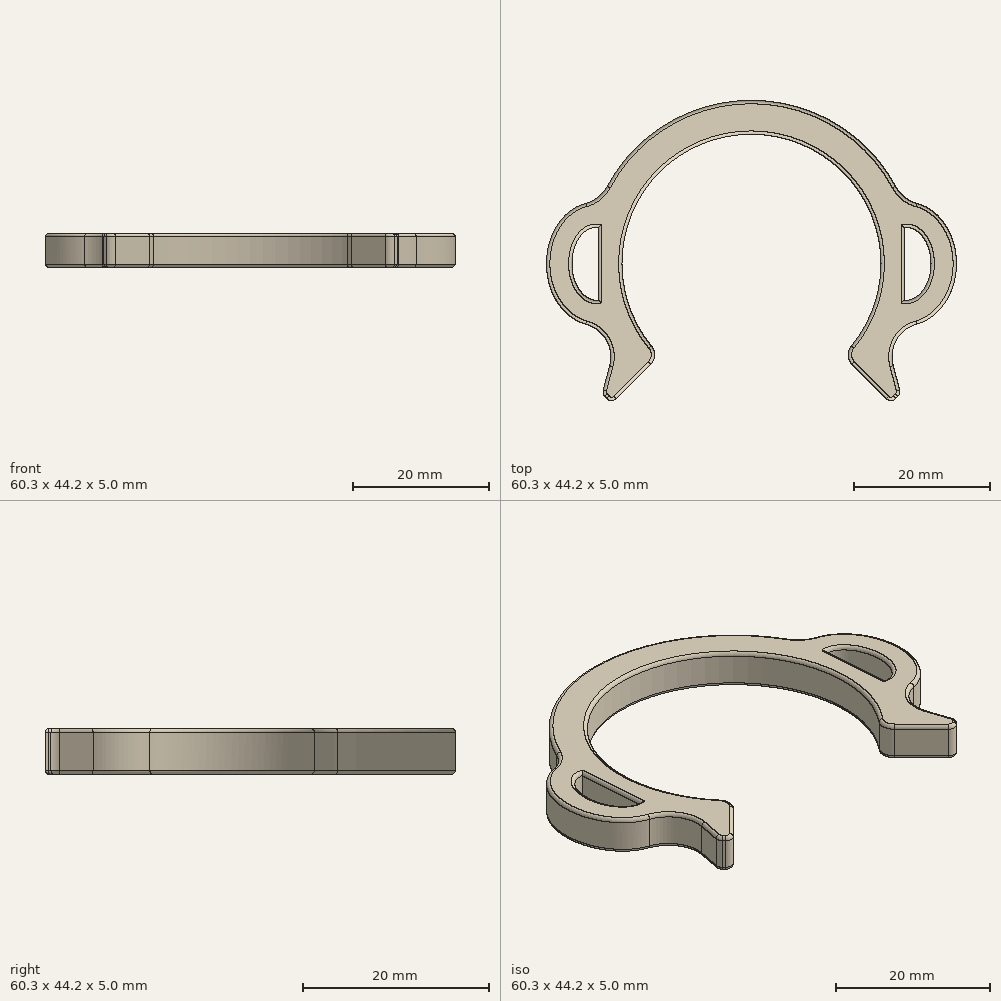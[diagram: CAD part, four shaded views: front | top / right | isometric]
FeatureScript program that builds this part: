
annotation { "Feature Type Name" : "Feature", "Feature Type Description" : "" }
export const myFeature = defineFeature(function(context is Context, id is Id, definition is map)
    precondition{}
    {
        {
            var Q0;
            Q0=qCreatedBy(makeId("Top.planeOp"),FACE);
            var sketch = newSketch(context, id + "F0", { "sketchPlane" : qUnion([Q0])});
            skCircle(sketch, "E0", {"center": v(0, 0) * mm, "radius": 18.75 * mm, "construction": true});
            skLineSegment(sketch, "E1", {"start": v(-22.75, 5.1) * mm, "end": v(-22.75, -5.1) * mm, "construction": true});
            skEllipticalArc(sketch, "E2", {"construction": true});
            skPoint(sketch, "E3", {"position": v(-22.75, 5.1) * mm});
            skPoint(sketch, "E4", {"position": v(-22.75, -5.1) * mm});
            skPoint(sketch, "E5", {"position": v(-26.15, 0) * mm});
            skLineSegment(sketch, "E6", {"start": v(0, 0) * mm, "end": v(0, 18.75) * mm, "construction": true});
            skEllipticalArc(sketch, "E7.MirrorCS", {"construction": true});
            skLineSegment(sketch, "E8.MirrorCS", {"start": v(22.75, 5.1) * mm, "end": v(22.75, -5.1) * mm, "construction": true});
            skCircle(sketch, "E9", {"center": v(-4, -23.75) * mm, "radius": 0.83 * mm, "construction": true});
            skArc(sketch, "E10", {"start": v(-13.47, -13.47) * mm, "mid": v(0, 19.05) * mm, "end": v(13.47, -13.47) * mm});
            skPoint(sketch, "E11", {"position": v(0, 19.05) * mm});
            skArc(sketch, "E12", {"start": v(0, 24.05) * mm, "mid": v(-12.35, 20.64) * mm, "end": v(-21.2, 11.36) * mm});
            skEllipticalArc(sketch, "E13", {});
            skPoint(sketch, "E14", {"position": v(-30.15, 0) * mm});
            skPoint(sketch, "E15", {"position": v(-22.75, 9.1) * mm});
            skLineSegment(sketch, "E16", {"start": v(-22.75, 5.1) * mm, "end": v(-22.75, 9.1) * mm, "construction": true});
            skLineSegment(sketch, "E17", {"start": v(-26.15, 0) * mm, "end": v(-30.15, 0) * mm, "construction": true});
            skPoint(sketch, "E18.visualSharp", {"position": v(-22.27, 9.08) * mm});
            skArc(sketch, "E18.filletArc", {"start": v(-24.32, 8.9) * mm, "mid": v(-22.5, 9.8) * mm, "end": v(-21.2, 11.36) * mm});
            skLineSegment(sketch, "E19.1", {"start": v(-22.5, 5.35) * mm, "end": v(-22.5, -5.35) * mm});
            skLineSegment(sketch, "E20", {"start": v(-13.47, -13.47) * mm, "end": v(-20.54, -20.54) * mm});
            skLineSegment(sketch, "E21", {"start": v(-20.54, -20.54) * mm, "end": v(-21.96, -19.13) * mm});
            skLineSegment(sketch, "E22", {"start": v(-21.96, -19.13) * mm, "end": v(-20.85, -15) * mm});
            skPoint(sketch, "E23.visualSharp", {"position": v(-18.92, -7.78) * mm});
            skArc(sketch, "E23.filletArc", {"start": v(-20.85, -15) * mm, "mid": v(-21.34, -11.22) * mm, "end": v(-24.36, -8.88) * mm});
            skArc(sketch, "E24.MirrorCS", {"start": v(0, 24.05) * mm, "mid": v(12.35, 20.64) * mm, "end": v(21.2, 11.36) * mm});
            skArc(sketch, "E25.MirrorCS", {"start": v(24.32, 8.9) * mm, "mid": v(22.5, 9.8) * mm, "end": v(21.2, 11.36) * mm});
            skEllipticalArc(sketch, "E26.MirrorCS", {});
            skArc(sketch, "E27.MirrorCS", {"start": v(20.85, -15) * mm, "mid": v(21.34, -11.22) * mm, "end": v(24.36, -8.88) * mm});
            skLineSegment(sketch, "E28.MirrorCS", {"start": v(21.96, -19.13) * mm, "end": v(20.85, -15) * mm});
            skLineSegment(sketch, "E29.MirrorCS", {"start": v(20.54, -20.54) * mm, "end": v(21.96, -19.13) * mm});
            skLineSegment(sketch, "E30.MirrorCS", {"start": v(13.47, -13.47) * mm, "end": v(20.54, -20.54) * mm});
            skLineSegment(sketch, "E31.MirrorCS", {"start": v(22.5, 5.35) * mm, "end": v(22.5, -5.35) * mm});
            skEllipticalArc(sketch, "E32", {});
            skLineSegment(sketch, "E33", {"start": v(26.4, 0) * mm, "end": v(26.15, 0) * mm, "construction": true});
            skLineSegment(sketch, "E34", {"start": v(22.75, 0) * mm, "end": v(22.5, 0) * mm, "construction": true});
            skLineSegment(sketch, "E35", {"start": v(-22.75, 0) * mm, "end": v(-22.5, 0) * mm, "construction": true});
            skEllipticalArc(sketch, "E36", {});
            skPoint(sketch, "E37", {"position": v(-26.4, 0) * mm});
            skCircle(sketch, "E38", {"center": v(4, -23.75) * mm, "radius": 0.83 * mm, "construction": true});
            skLineSegment(sketch, "E39", {"start": v(-4, -23.75) * mm, "end": v(4, -23.75) * mm, "construction": true});
            skLineSegment(sketch, "E40", {"start": v(0, 0) * mm, "end": v(0, -23.75) * mm, "construction": true});
            skPoint(sketch, "E41", {"position": v(0, -18.75) * mm});
            const initialGuessF0  = {"E2": [-0.02275, 0, 0, -1, 0.0051, 0.0034, 3.141592653589793, 0], "E7.MirrorCS": [0.02275, 0, 0, -1, 0.0051, 0.0034, 0, 3.141592653589793], "E13": [-0.02275, 0, 0, 1, 0.0091, 0.0074, 0.21327389126291205, 2.922477853467835], "E26.MirrorCS": [0.02275, 0, 0, 1, 0.0091, 0.0074, 3.3607074537117514, 6.069911415916674], "E32": [0.02275, 0, 0, 1, 0.005362593586465865, 0.00365, 3.073045835744844, 0.06854681784494943], "E36": [-0.02275, 0, 0, 1, 0.005362593586465865, 0.00365, 6.214638489334637, 3.210139471434742]};
            skSetInitialGuess(sketch, initialGuessF0);
            skSolve(sketch);
        }
        {
            var Q0;
            Q0 = qSketchRegion(id + "F0", true);
            extrude(context, id + "F1", {"entities" : qUnion([Q0]), "depth" : 5 * mm});
        }
        {
            var Q0;
            Q0=makeQuery(id+"F1.opExtrude","SWEPT_EDGE",EDGE,{"disambiguationData":[OSD([sQuery(id+"F0.wireOp",EDGE,"E10"),sQuery(id+"F0.wireOp",EDGE,"E20")])]});
            var Q1;
            Q1=makeQuery(id+"F1.opExtrude","SWEPT_EDGE",EDGE,{"disambiguationData":[OSD([sQuery(id+"F0.wireOp",EDGE,"E10"),sQuery(id+"F0.wireOp",EDGE,"E30.MirrorCS")])]});
            fillet(context, id + "F2", {"entities" : qUnion([Q0, Q1]), "radius" : 2 * mm, "tangentPropagation" : true, "allowEdgeOverflow" : false});
        }
        {
            var Q0;
            Q0=makeQuery(id+"F1.opExtrude","SWEPT_EDGE",EDGE,{"disambiguationData":[OSD([sQuery(id+"F0.wireOp",EDGE,"E20"),sQuery(id+"F0.wireOp",EDGE,"E21")])]});
            var Q1;
            Q1=makeQuery(id+"F1.opExtrude","SWEPT_EDGE",EDGE,{"disambiguationData":[OSD([sQuery(id+"F0.wireOp",EDGE,"E21"),sQuery(id+"F0.wireOp",EDGE,"E22")])]});
            var Q2;
            Q2=makeQuery(id+"F1.opExtrude","SWEPT_EDGE",EDGE,{"disambiguationData":[OSD([sQuery(id+"F0.wireOp",EDGE,"E28.MirrorCS"),sQuery(id+"F0.wireOp",EDGE,"E29.MirrorCS")])]});
            var Q3;
            Q3=makeQuery(id+"F1.opExtrude","SWEPT_EDGE",EDGE,{"disambiguationData":[OSD([sQuery(id+"F0.wireOp",EDGE,"E29.MirrorCS"),sQuery(id+"F0.wireOp",EDGE,"E30.MirrorCS")])]});
            fillet(context, id + "F3", {"entities" : qUnion([Q0, Q1, Q2, Q3]), "radius" : 1 * mm, "tangentPropagation" : true, "allowEdgeOverflow" : false});
        }
        {
            var Q0;
            Q0=makeQuery(id+"F1.opExtrude","CAP_FACE",FACE,{"disambiguationData":[OSD([sQuery(id+"F0.wireOp",EDGE,"E10"),sQuery(id+"F0.wireOp",EDGE,"E12"),sQuery(id+"F0.wireOp",EDGE,"E13"),sQuery(id+"F0.wireOp",EDGE,"E18.filletArc"),sQuery(id+"F0.wireOp",EDGE,"E19.1"),sQuery(id+"F0.wireOp",EDGE,"E20"),sQuery(id+"F0.wireOp",EDGE,"E21"),sQuery(id+"F0.wireOp",EDGE,"E22"),sQuery(id+"F0.wireOp",EDGE,"E23.filletArc"),sQuery(id+"F0.wireOp",EDGE,"E24.MirrorCS"),sQuery(id+"F0.wireOp",EDGE,"E25.MirrorCS"),sQuery(id+"F0.wireOp",EDGE,"E26.MirrorCS"),sQuery(id+"F0.wireOp",EDGE,"E27.MirrorCS"),sQuery(id+"F0.wireOp",EDGE,"E28.MirrorCS"),sQuery(id+"F0.wireOp",EDGE,"E29.MirrorCS"),sQuery(id+"F0.wireOp",EDGE,"E30.MirrorCS"),sQuery(id+"F0.wireOp",EDGE,"E31.MirrorCS"),sQuery(id+"F0.wireOp",EDGE,"E32"),sQuery(id+"F0.wireOp",EDGE,"E36")])],"isStart":true});
            var Q1;
            Q1=makeQuery(id+"F1.opExtrude","CAP_FACE",FACE,{"disambiguationData":[OSD([sQuery(id+"F0.wireOp",EDGE,"E10"),sQuery(id+"F0.wireOp",EDGE,"E12"),sQuery(id+"F0.wireOp",EDGE,"E13"),sQuery(id+"F0.wireOp",EDGE,"E18.filletArc"),sQuery(id+"F0.wireOp",EDGE,"E19.1"),sQuery(id+"F0.wireOp",EDGE,"E20"),sQuery(id+"F0.wireOp",EDGE,"E21"),sQuery(id+"F0.wireOp",EDGE,"E22"),sQuery(id+"F0.wireOp",EDGE,"E23.filletArc"),sQuery(id+"F0.wireOp",EDGE,"E24.MirrorCS"),sQuery(id+"F0.wireOp",EDGE,"E25.MirrorCS"),sQuery(id+"F0.wireOp",EDGE,"E26.MirrorCS"),sQuery(id+"F0.wireOp",EDGE,"E27.MirrorCS"),sQuery(id+"F0.wireOp",EDGE,"E28.MirrorCS"),sQuery(id+"F0.wireOp",EDGE,"E29.MirrorCS"),sQuery(id+"F0.wireOp",EDGE,"E30.MirrorCS"),sQuery(id+"F0.wireOp",EDGE,"E31.MirrorCS"),sQuery(id+"F0.wireOp",EDGE,"E32"),sQuery(id+"F0.wireOp",EDGE,"E36")])],"isStart":false});
            fillet(context, id + "F4", {"entities" : qUnion([Q0, Q1]), "radius" : 0.5 * mm, "tangentPropagation" : true, "allowEdgeOverflow" : false});
        }
    });
